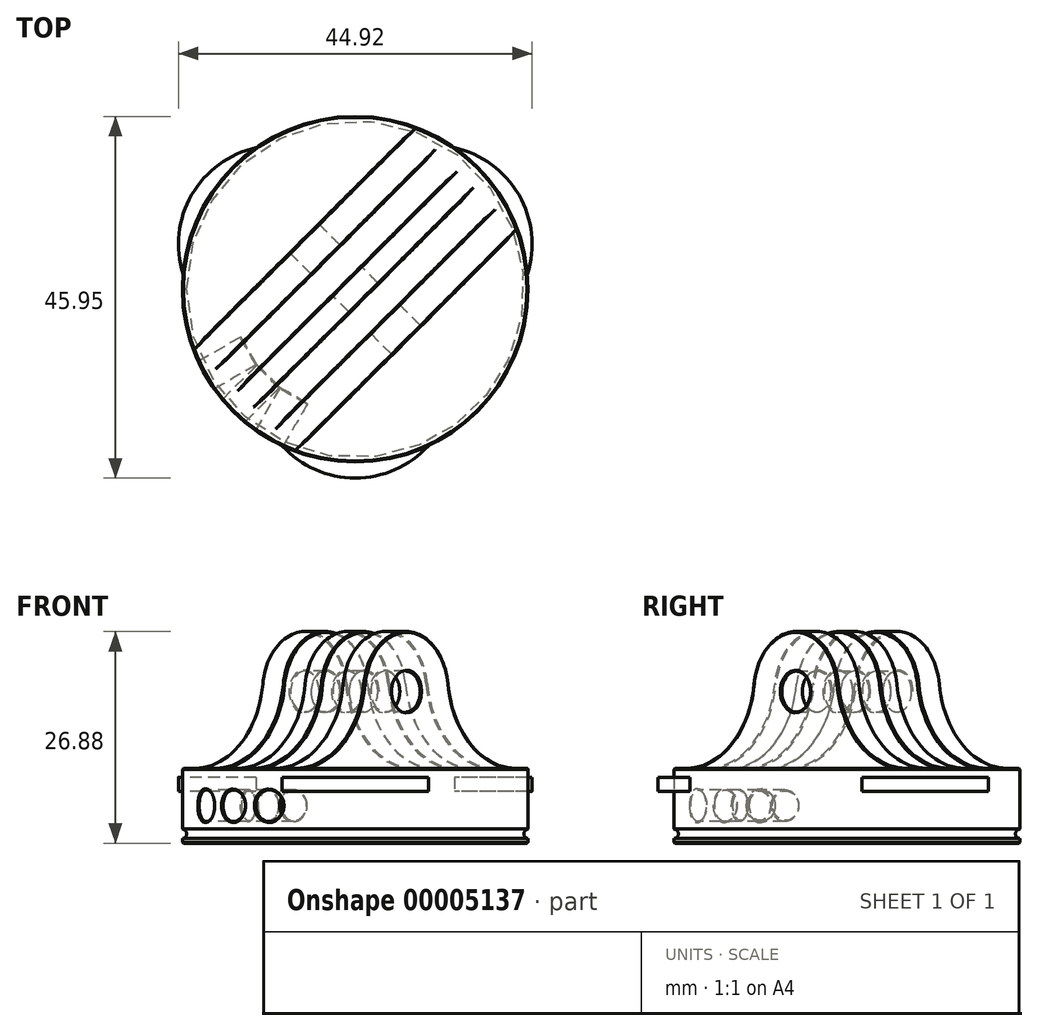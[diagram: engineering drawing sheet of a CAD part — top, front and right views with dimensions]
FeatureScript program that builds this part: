
annotation { "Feature Type Name" : "Feature", "Feature Type Description" : "" }
export const myFeature = defineFeature(function(context is Context, id is Id, definition is map)
    precondition{}
    {
        {
            var Q0;
            Q0=qCreatedBy(makeId("Top.planeOp"),FACE);
            var sketch = newSketch(context, id + "F0", { "sketchPlane" : qUnion([Q0])});
            skCircle(sketch, "E0", {"center": v(0, 0) * mm, "radius": 21.96 * mm});
            skLineSegment(sketch, "E1", {"start": v(0, 0) * mm, "end": v(0, -33.51) * mm, "construction": true});
            skLineSegment(sketch, "E2", {"start": v(0, 0) * mm, "end": v(-37.19, 21.47) * mm, "construction": true});
            skLineSegment(sketch, "E3", {"start": v(0, 0) * mm, "end": v(-19.02, -10.98) * mm, "construction": true});
            skArc(sketch, "E4", {"start": v(-9.28, -19.9) * mm, "mid": v(0, -24) * mm, "end": v(9.28, -19.9) * mm});
            skArc(sketch, "E5.2.0", {"start": v(-12.6, 17.99) * mm, "mid": v(-20.78, 12) * mm, "end": v(-21.87, 1.92) * mm});
            skArc(sketch, "E6.trimOffspring", {"start": v(21.87, 1.92) * mm, "mid": v(20.78, 12) * mm, "end": v(12.6, 17.99) * mm});
            skLineSegment(sketch, "E7", {"start": v(0, 0) * mm, "end": v(-15.53, -15.53) * mm, "construction": true});
            skLineSegment(sketch, "E8", {"start": v(0, 0) * mm, "end": v(-10.98, -19.02) * mm, "construction": true});
            skLineSegment(sketch, "E9", {"start": v(0, 0) * mm, "end": v(15.53, -15.53) * mm, "construction": true});
            skSolve(sketch);
        }
        {
            var Q0;
            {var subQ0=sQuery(id+"F0.wireOp",EDGE,"E0");var subQ1=sQuery(id+"F0.wireOp",EDGE,"E6.trimOffspring");var subQ2=makeQuery(id+"F0.imprint","INTERSECT",VERTEX,{"disambiguationData":[OD(0.0)],"derivedFrom":[subQ0,subQ1]});Q0=makeQuery(id+"F0.imprint","IMPRINT",FACE,{"disambiguationData":[TD([[makeQuery(id+"F0.imprint","IMPRINT",EDGE,{"disambiguationData":[TD([[subQ2,-1.0]])],"derivedFrom":subQ0}),1.0]])]});}
            extrude(context, id + "F1", {"entities" : qUnion([Q0]), "depth" : 9.52 * mm, "symmetric" : true});
        }
        {
            var Q0;
            {var subQ0=sQuery(id+"F0.wireOp",EDGE,"E5.2.0");Q0=makeQuery(id+"F0.imprint","IMPRINT",FACE,{"disambiguationData":[TD([[makeQuery(id+"F0.imprint","IMPRINT",EDGE,{"derivedFrom":subQ0}),1.0]])]});}
            var Q1;
            {var subQ0=sQuery(id+"F0.wireOp",EDGE,"E6.trimOffspring");Q1=makeQuery(id+"F0.imprint","IMPRINT",FACE,{"disambiguationData":[TD([[makeQuery(id+"F0.imprint","IMPRINT",EDGE,{"derivedFrom":subQ0}),1.0]])]});}
            var Q2;
            {var subQ0=sQuery(id+"F0.wireOp",EDGE,"E4");Q2=makeQuery(id+"F0.imprint","IMPRINT",FACE,{"disambiguationData":[TD([[makeQuery(id+"F0.imprint","IMPRINT",EDGE,{"derivedFrom":subQ0}),1.0]])]});}
            extrude(context, id + "F2", {"entities" : qUnion([Q0, Q1, Q2]), "depth" : 1.78 * mm});
        }
        {
            var Q0;
            Q0=makeQuery(id+"F2.opExtrude","SWEPT_BODY",BODY,{"disambiguationData":[OSD([sQuery(id+"F0.wireOp",EDGE,"E0"),sQuery(id+"F0.wireOp",EDGE,"E6.trimOffspring")])]});
            var Q1;
            Q1=makeQuery(id+"F2.opExtrude","SWEPT_BODY",BODY,{"disambiguationData":[OSD([sQuery(id+"F0.wireOp",EDGE,"E0"),sQuery(id+"F0.wireOp",EDGE,"E5.2.0")])]});
            var Q2;
            Q2=makeQuery(id+"F2.opExtrude","SWEPT_BODY",BODY,{"disambiguationData":[OSD([sQuery(id+"F0.wireOp",EDGE,"E0"),sQuery(id+"F0.wireOp",EDGE,"E4")])]});
            var Q3;
            Q3=makeQuery(id+"F1.opExtrude","CAP_FACE",FACE,{"disambiguationData":[OSD([sQuery(id+"F0.wireOp",EDGE,"E0")])],"isStart":false});
            var Q4;
            Q4=qCreatedBy(makeId("Top.planeOp"),FACE);
            transform(context, id + "F3", {"entities" : qUnion([Q0, Q1, Q2]), "transformType" : TransformType.TRANSLATION_DISTANCE, "transformDirection" : qUnion([Q3, Q4]), "distance" : 1.84 * mm, "makeCopy" : false});
        }
        {
            var Q0;
            Q0=sQuery(id+"F0.wireOp",VERTEX,"E3.end");
            var Q1;
            Q1=sQuery(id+"F0.wireOp",EDGE,"E3");
            cPlane(context, id + "F4", {"entities" : qUnion([Q0, Q1]), "cplaneType" : CPlaneType.LINE_POINT, "offset" : 21.93 * mm, "width" : 152.4 * mm, "height" : 152.4 * mm});
        }
        {
            var Q0;
            Q0=sQuery(id+"F0.wireOp",EDGE,"E7");
            var Q1;
            Q1=sQuery(id+"F0.wireOp",VERTEX,"E7.end");
            cPlane(context, id + "F5", {"entities" : qUnion([Q0, Q1]), "cplaneType" : CPlaneType.LINE_POINT, "offset" : 152.4 * mm, "width" : 152.4 * mm, "height" : 152.4 * mm});
        }
        {
            var Q0;
            Q0=sQuery(id+"F0.wireOp",EDGE,"E8");
            var Q1;
            Q1=sQuery(id+"F0.wireOp",VERTEX,"E8.end");
            cPlane(context, id + "F6", {"entities" : qUnion([Q0, Q1]), "cplaneType" : CPlaneType.LINE_POINT, "offset" : 152.4 * mm, "width" : 152.4 * mm, "height" : 152.4 * mm});
        }
        {
            var Q0;
            Q0=qCreatedBy(id+"F4.planeOp",FACE);
            var sketch = newSketch(context, id + "F7", { "sketchPlane" : qUnion([Q0])});
            skCircle(sketch, "E10", {"center": v(0, 0) * mm, "radius": 2.02 * mm});
            skSolve(sketch);
        }
        {
            var Q0;
            Q0=makeQuery(id+"F7.imprint","IMPRINT",FACE,{"disambiguationData":[TD([[makeQuery(id+"F7.imprint","IMPRINT",EDGE,{"derivedFrom":sQuery(id+"F7.wireOp",EDGE,"E10")}),1.0]])]});
            extrude(context, id + "F8", {"entities" : qUnion([Q0]), "operationType" : NewBodyOperationType.REMOVE, "oppositeDirection" : true, "depth" : 12.7 * mm, "symmetric" : true});
        }
        {
            var Q0;
            Q0=qCreatedBy(id+"F5.planeOp",FACE);
            var sketch = newSketch(context, id + "F9", { "sketchPlane" : qUnion([Q0])});
            skCircle(sketch, "E11", {"center": v(0, 0) * mm, "radius": 2.02 * mm});
            skSolve(sketch);
        }
        {
            var Q0;
            Q0=makeQuery(id+"F9.imprint","IMPRINT",FACE,{"disambiguationData":[TD([[makeQuery(id+"F9.imprint","IMPRINT",EDGE,{"derivedFrom":sQuery(id+"F9.wireOp",EDGE,"E11")}),1.0]])]});
            extrude(context, id + "F10", {"entities" : qUnion([Q0]), "operationType" : NewBodyOperationType.REMOVE, "oppositeDirection" : true, "depth" : 12.7 * mm, "symmetric" : true});
        }
        {
            var Q0;
            Q0=qCreatedBy(id+"F6.planeOp",FACE);
            var sketch = newSketch(context, id + "F11", { "sketchPlane" : qUnion([Q0])});
            skCircle(sketch, "E12", {"center": v(0, 0) * mm, "radius": 2.02 * mm});
            skSolve(sketch);
        }
        {
            var Q0;
            Q0=makeQuery(id+"F11.imprint","IMPRINT",FACE,{"disambiguationData":[TD([[makeQuery(id+"F11.imprint","IMPRINT",EDGE,{"derivedFrom":sQuery(id+"F11.wireOp",EDGE,"E12")}),1.0]])]});
            extrude(context, id + "F12", {"entities" : qUnion([Q0]), "operationType" : NewBodyOperationType.REMOVE, "oppositeDirection" : true, "depth" : 12.7 * mm, "symmetric" : true});
        }
        {
            var Q0;
            Q0=sQuery(id+"F0.wireOp",VERTEX,"E9.end");
            var Q1;
            Q1=sQuery(id+"F0.wireOp",EDGE,"E9");
            cPlane(context, id + "F13", {"entities" : qUnion([Q0, Q1]), "cplaneType" : CPlaneType.LINE_POINT, "offset" : 152.4 * mm, "width" : 152.4 * mm, "height" : 152.4 * mm});
        }
        {
            var Q0;
            Q0=qCreatedBy(id+"F13.planeOp",FACE);
            cPlane(context, id + "F14", {"entities" : qUnion([Q0]), "cplaneType" : CPlaneType.OFFSET, "offset" : 21.93 * mm, "oppositeDirection" : true, "width" : 152.4 * mm, "height" : 152.4 * mm});
        }
        {
            var Q0;
            Q0=qCreatedBy(id+"F14.planeOp",FACE);
            var sketch = newSketch(context, id + "F15", { "sketchPlane" : qUnion([Q0])});
            skLineSegment(sketch, "E13", {"start": v(-24.14, 4.76) * mm, "end": v(19.73, 4.76) * mm});
            skCircle(sketch, "E14", {"center": v(0, 14.5) * mm, "radius": 7.62 * mm});
            skCircle(sketch, "E15", {"center": v(0, 14.5) * mm, "radius": 2.6 * mm});
            skArc(sketch, "E16", {"start": v(-19.73, 4.76) * mm, "mid": v(-11.62, 7.82) * mm, "end": v(-7.56, 15.47) * mm});
            skArc(sketch, "E17", {"start": v(7.56, 15.47) * mm, "mid": v(11.62, 7.82) * mm, "end": v(19.73, 4.76) * mm});
            skSolve(sketch);
        }
        {
            var Q0;
            {var subQ1=sQuery(id+"F15.wireOp",EDGE,"E16");Q0=makeQuery(id+"F15.imprint","IMPRINT",FACE,{"disambiguationData":[TD([[makeQuery(id+"F15.imprint","IMPRINT",EDGE,{"derivedFrom":subQ1}),-1.0]])]});}
            var Q1;
            Q1=makeQuery(id+"F15.imprint","IMPRINT",FACE,{"disambiguationData":[TD([[makeQuery(id+"F15.imprint","IMPRINT",EDGE,{"derivedFrom":sQuery(id+"F15.wireOp",EDGE,"E15")}),-1.0]])]});
            extrude(context, id + "F16", {"entities" : qUnion([Q0, Q1]), "operationType" : NewBodyOperationType.ADD, "depth" : 18.4 * mm, "symmetric" : true});
        }
        {
            var Q0;
            Q0=qCreatedBy(id+"F5.planeOp",FACE);
            cPlane(context, id + "F17", {"entities" : qUnion([Q0]), "cplaneType" : CPlaneType.OFFSET, "offset" : 21.93 * mm, "oppositeDirection" : true, "width" : 152.4 * mm, "height" : 152.4 * mm});
        }
        {
            var Q0;
            Q0=qCreatedBy(id+"F17.planeOp",FACE);
            var sketch = newSketch(context, id + "F18", { "sketchPlane" : qUnion([Q0])});
            skLineSegment(sketch, "E18.bottom", {"start": v(5.28, 4.76) * mm, "end": v(1.6, 4.76) * mm});
            skLineSegment(sketch, "E18.top", {"start": v(5.28, 26.99) * mm, "end": v(1.6, 26.99) * mm});
            skLineSegment(sketch, "E18.left", {"start": v(5.28, 4.76) * mm, "end": v(5.28, 26.99) * mm});
            skLineSegment(sketch, "E18.right", {"start": v(1.6, 4.76) * mm, "end": v(1.6, 26.99) * mm});
            skLineSegment(sketch, "E19.bottom", {"start": v(-1.55, 4.76) * mm, "end": v(-5.23, 4.76) * mm});
            skLineSegment(sketch, "E19.top", {"start": v(-1.55, 27.39) * mm, "end": v(-5.23, 27.39) * mm});
            skLineSegment(sketch, "E19.left", {"start": v(-1.55, 4.76) * mm, "end": v(-1.55, 27.39) * mm});
            skLineSegment(sketch, "E19.right", {"start": v(-5.23, 4.76) * mm, "end": v(-5.23, 27.39) * mm});
            skSolve(sketch);
        }
        {
            var Q0;
            Q0=makeQuery(id+"F18.imprint","IMPRINT",FACE,{"disambiguationData":[TD([[makeQuery(id+"F18.imprint","IMPRINT",EDGE,{"derivedFrom":sQuery(id+"F18.wireOp",EDGE,"E18.bottom")}),-1.0]])]});
            var Q1;
            Q1=makeQuery(id+"F18.imprint","IMPRINT",FACE,{"disambiguationData":[TD([[makeQuery(id+"F18.imprint","IMPRINT",EDGE,{"derivedFrom":sQuery(id+"F18.wireOp",EDGE,"E19.bottom")}),-1.0]])]});
            extrude(context, id + "F19", {"entities" : qUnion([Q0, Q1]), "operationType" : NewBodyOperationType.REMOVE, "oppositeDirection" : true, "depth" : 50.8 * mm, "symmetric" : true});
        }
        {
            var Q0;
            Q0=makeQuery(id+"F12.boolean.opBoolean","COPY",FACE,{"derivedFrom":makeQuery(id+"F12.opExtrude","SWEPT_FACE",FACE,{"disambiguationData":[OSD([sQuery(id+"F11.wireOp",EDGE,"E12")])]})});
            var Q1;
            Q1=makeQuery(id+"F10.boolean.opBoolean","COPY",FACE,{"derivedFrom":makeQuery(id+"F10.opExtrude","SWEPT_FACE",FACE,{"disambiguationData":[OSD([sQuery(id+"F9.wireOp",EDGE,"E11")])]})});
            var Q2;
            Q2=makeQuery(id+"F8.boolean.opBoolean","COPY",FACE,{"derivedFrom":makeQuery(id+"F8.opExtrude","SWEPT_FACE",FACE,{"disambiguationData":[OSD([sQuery(id+"F7.wireOp",EDGE,"E10")])]})});
            var Q3;
            Q3=makeQuery(id+"F19.boolean.opBoolean","INTERSECT",EDGE,{"derivedFrom":[makeQuery(id+"F16.opExtrude","SWEPT_FACE",FACE,{"disambiguationData":[OSD([sQuery(id+"F15.wireOp",EDGE,"E16")])]}),makeQuery(id+"F19.opExtrude","SWEPT_FACE",FACE,{"disambiguationData":[OSD([sQuery(id+"F18.wireOp",EDGE,"E18.left")])]})]});
            var Q4;
            Q4=makeQuery(id+"F19.boolean.opBoolean","INTERSECT",EDGE,{"derivedFrom":[makeQuery(id+"F16.opExtrude","SWEPT_FACE",FACE,{"disambiguationData":[OSD([sQuery(id+"F15.wireOp",EDGE,"E14")])]}),makeQuery(id+"F19.opExtrude","SWEPT_FACE",FACE,{"disambiguationData":[OSD([sQuery(id+"F18.wireOp",EDGE,"E18.right")])]})]});
            var Q5;
            Q5=makeQuery(id+"F19.boolean.opBoolean","INTERSECT",EDGE,{"derivedFrom":[makeQuery(id+"F16.opExtrude","SWEPT_FACE",FACE,{"disambiguationData":[OSD([sQuery(id+"F15.wireOp",EDGE,"E14")])]}),makeQuery(id+"F19.opExtrude","SWEPT_FACE",FACE,{"disambiguationData":[OSD([sQuery(id+"F18.wireOp",EDGE,"E18.left")])]})]});
            var Q6;
            Q6=makeQuery(id+"F19.boolean.opBoolean","INTERSECT",EDGE,{"derivedFrom":[makeQuery(id+"F16.opExtrude","SWEPT_FACE",FACE,{"disambiguationData":[OSD([sQuery(id+"F15.wireOp",EDGE,"E16")])]}),makeQuery(id+"F19.opExtrude","SWEPT_FACE",FACE,{"disambiguationData":[OSD([sQuery(id+"F18.wireOp",EDGE,"E18.right")])]})]});
            var Q7;
            Q7=makeQuery(id+"F19.boolean.opBoolean","INTERSECT",EDGE,{"derivedFrom":[makeQuery(id+"F16.opExtrude","SWEPT_FACE",FACE,{"disambiguationData":[OSD([sQuery(id+"F15.wireOp",EDGE,"E16")])]}),makeQuery(id+"F19.opExtrude","SWEPT_FACE",FACE,{"disambiguationData":[OSD([sQuery(id+"F18.wireOp",EDGE,"E19.left")])]})]});
            var Q8;
            Q8=makeQuery(id+"F19.boolean.opBoolean","INTERSECT",EDGE,{"derivedFrom":[makeQuery(id+"F16.opExtrude","SWEPT_FACE",FACE,{"disambiguationData":[OSD([sQuery(id+"F15.wireOp",EDGE,"E14")])]}),makeQuery(id+"F19.opExtrude","SWEPT_FACE",FACE,{"disambiguationData":[OSD([sQuery(id+"F18.wireOp",EDGE,"E19.left")])]})]});
            var Q9;
            Q9=makeQuery(id+"F19.boolean.opBoolean","INTERSECT",EDGE,{"derivedFrom":[makeQuery(id+"F16.opExtrude","SWEPT_FACE",FACE,{"disambiguationData":[OSD([sQuery(id+"F15.wireOp",EDGE,"E14")])]}),makeQuery(id+"F19.opExtrude","SWEPT_FACE",FACE,{"disambiguationData":[OSD([sQuery(id+"F18.wireOp",EDGE,"E19.right")])]})]});
            var Q10;
            Q10=makeQuery(id+"F19.boolean.opBoolean","INTERSECT",EDGE,{"derivedFrom":[makeQuery(id+"F16.opExtrude","SWEPT_FACE",FACE,{"disambiguationData":[OSD([sQuery(id+"F15.wireOp",EDGE,"E16")])]}),makeQuery(id+"F19.opExtrude","SWEPT_FACE",FACE,{"disambiguationData":[OSD([sQuery(id+"F18.wireOp",EDGE,"E19.right")])]})]});
            var Q11;
            Q11=makeQuery(id+"F19.boolean.opBoolean","INTERSECT",EDGE,{"derivedFrom":[makeQuery(id+"F16.opExtrude","SWEPT_FACE",FACE,{"disambiguationData":[OSD([sQuery(id+"F15.wireOp",EDGE,"E17")])]}),makeQuery(id+"F19.opExtrude","SWEPT_FACE",FACE,{"disambiguationData":[OSD([sQuery(id+"F18.wireOp",EDGE,"E19.right")])]})]});
            var Q12;
            Q12=makeQuery(id+"F19.boolean.opBoolean","INTERSECT",EDGE,{"derivedFrom":[makeQuery(id+"F16.opExtrude","SWEPT_FACE",FACE,{"disambiguationData":[OSD([sQuery(id+"F15.wireOp",EDGE,"E17")])]}),makeQuery(id+"F19.opExtrude","SWEPT_FACE",FACE,{"disambiguationData":[OSD([sQuery(id+"F18.wireOp",EDGE,"E19.left")])]})]});
            var Q13;
            Q13=makeQuery(id+"F19.boolean.opBoolean","INTERSECT",EDGE,{"derivedFrom":[makeQuery(id+"F16.opExtrude","SWEPT_FACE",FACE,{"disambiguationData":[OSD([sQuery(id+"F15.wireOp",EDGE,"E17")])]}),makeQuery(id+"F19.opExtrude","SWEPT_FACE",FACE,{"disambiguationData":[OSD([sQuery(id+"F18.wireOp",EDGE,"E18.right")])]})]});
            var Q14;
            Q14=makeQuery(id+"F19.boolean.opBoolean","INTERSECT",EDGE,{"derivedFrom":[makeQuery(id+"F16.opExtrude","SWEPT_FACE",FACE,{"disambiguationData":[OSD([sQuery(id+"F15.wireOp",EDGE,"E17")])]}),makeQuery(id+"F19.opExtrude","SWEPT_FACE",FACE,{"disambiguationData":[OSD([sQuery(id+"F18.wireOp",EDGE,"E18.left")])]})]});
            var Q15;
            Q15=makeQuery(id+"F16.opExtrude","CAP_EDGE",EDGE,{"disambiguationData":[OSD([sQuery(id+"F15.wireOp",EDGE,"E17")])],"isStart":false});
            var Q16;
            Q16=makeQuery(id+"F16.opExtrude","CAP_EDGE",EDGE,{"disambiguationData":[OSD([sQuery(id+"F15.wireOp",EDGE,"E14")])],"isStart":false});
            var Q17;
            Q17=makeQuery(id+"F16.opExtrude","CAP_EDGE",EDGE,{"disambiguationData":[OSD([sQuery(id+"F15.wireOp",EDGE,"E16")])],"isStart":false});
            var Q18;
            Q18=makeQuery(id+"F16.opExtrude","CAP_EDGE",EDGE,{"disambiguationData":[OSD([sQuery(id+"F15.wireOp",EDGE,"E17")])],"isStart":true});
            var Q19;
            Q19=makeQuery(id+"F16.opExtrude","CAP_EDGE",EDGE,{"disambiguationData":[OSD([sQuery(id+"F15.wireOp",EDGE,"E14")])],"isStart":true});
            var Q20;
            Q20=makeQuery(id+"F16.opExtrude","CAP_EDGE",EDGE,{"disambiguationData":[OSD([sQuery(id+"F15.wireOp",EDGE,"E16")])],"isStart":true});
            var Q21;
            {var subQ0=sQuery(id+"F0.wireOp",EDGE,"E0");Q21=makeQuery(id+"Ff1VSCdrAeOWZMI_3.opShell","OFFSET_EDGE",EDGE,{"disambiguationData":[OSD([subQ0]),TDD([makeQuery(id+"F1.opExtrude","CAP_EDGE",EDGE,{"disambiguationData":[OSD([subQ0])],"isStart":true})])]});}
            var Q22;
            Q22=makeQuery(id+"F1.opExtrude","CAP_EDGE",EDGE,{"disambiguationData":[OSD([sQuery(id+"F0.wireOp",EDGE,"E0")])],"isStart":true});
            var Q23;
            {var subQ0=sQuery(id+"F15.wireOp",EDGE,"E15");Q23=makeQuery(id+"F19.boolean.opBoolean","SPLIT",FACE,{"disambiguationData":[TD([makeQuery(id+"F19.opExtrude","SWEPT_FACE",FACE,{"disambiguationData":[OSD([sQuery(id+"F18.wireOp",EDGE,"E18.left")])]})])],"derivedFrom":makeQuery(id+"F16.opExtrude","SWEPT_FACE",FACE,{"disambiguationData":[OSD([subQ0])]})});}
            var Q24;
            Q24=makeQuery(id+"F19.boolean.opBoolean","SPLIT",FACE,{"disambiguationData":[TD([makeQuery(id+"F19.opExtrude","SWEPT_FACE",FACE,{"disambiguationData":[OSD([sQuery(id+"F18.wireOp",EDGE,"E18.right")])]})])],"derivedFrom":makeQuery(id+"F16.opExtrude","SWEPT_FACE",FACE,{"disambiguationData":[OSD([sQuery(id+"F15.wireOp",EDGE,"E15")])]})});
            var Q25;
            {var subQ0=sQuery(id+"F15.wireOp",EDGE,"E15");Q25=makeQuery(id+"F19.boolean.opBoolean","SPLIT",FACE,{"disambiguationData":[TD([makeQuery(id+"F19.opExtrude","SWEPT_FACE",FACE,{"disambiguationData":[OSD([sQuery(id+"F18.wireOp",EDGE,"E19.right")])]})])],"derivedFrom":makeQuery(id+"F16.opExtrude","SWEPT_FACE",FACE,{"disambiguationData":[OSD([subQ0])]})});}
            var Q26;
            Q26=makeQuery(id+"F19.boolean.opBoolean","INTERSECT",EDGE,{"derivedFrom":[makeQuery(id+"F19.opExtrude","SWEPT_FACE",FACE,{"disambiguationData":[OSD([sQuery(id+"F18.wireOp",EDGE,"E18.bottom")])]}),makeQuery(id+"F19.opExtrude","SWEPT_FACE",FACE,{"disambiguationData":[OSD([sQuery(id+"F18.wireOp",EDGE,"E19.bottom")])]})]});
            chamfer(context, id + "F20", {"entities" : qUnion([Q0, Q1, Q2, Q3, Q4, Q5, Q6, Q7, Q8, Q9, Q10, Q11, Q12, Q13, Q14, Q15, Q16, Q17, Q18, Q19, Q20, Q21, Q22, Q23, Q24, Q25, Q26]), "width" : 0.13 * mm, "tangentPropagation" : true});
        }
        {
            var Q0;
            Q0=qCreatedBy(makeId("Front.planeOp"),FACE);
            var sketch = newSketch(context, id + "F21", { "sketchPlane" : qUnion([Q0])});
            skCircle(sketch, "E20", {"center": v(22, -3.57) * mm, "radius": 0.6 * mm});
            skSolve(sketch);
        }
        {
            var Q0;
            Q0=makeQuery(id+"F1.opExtrude","CAP_FACE",FACE,{"disambiguationData":[OSD([sQuery(id+"F0.wireOp",EDGE,"E0")])],"isStart":true});
            cPlane(context, id + "F22", {"entities" : qUnion([Q0]), "cplaneType" : CPlaneType.OFFSET, "offset" : 1.2 * mm, "oppositeDirection" : true, "width" : 152.4 * mm, "height" : 152.4 * mm});
        }
        {
            var Q0;
            Q0=qCreatedBy(id+"F22.planeOp",FACE);
            var sketch = newSketch(context, id + "F23", { "sketchPlane" : qUnion([Q0])});
            skCircle(sketch, "E21", {"center": v(0, 0) * mm, "radius": 21.96 * mm});
            skSolve(sketch);
        }
        {
            var Q0;
            Q0=makeQuery(id+"F21.imprint","IMPRINT",FACE,{"disambiguationData":[TD([[makeQuery(id+"F21.imprint","IMPRINT",EDGE,{"derivedFrom":sQuery(id+"F21.wireOp",EDGE,"E20")}),1.0]])]});
            var Q1;
            Q1=sQuery(id+"F23.wireOp",EDGE,"E21");
            sweep(context, id + "F24", {"operationType" : NewBodyOperationType.REMOVE, "profiles" : qUnion([Q0]), "path" : qUnion([Q1])});
        }
    });
